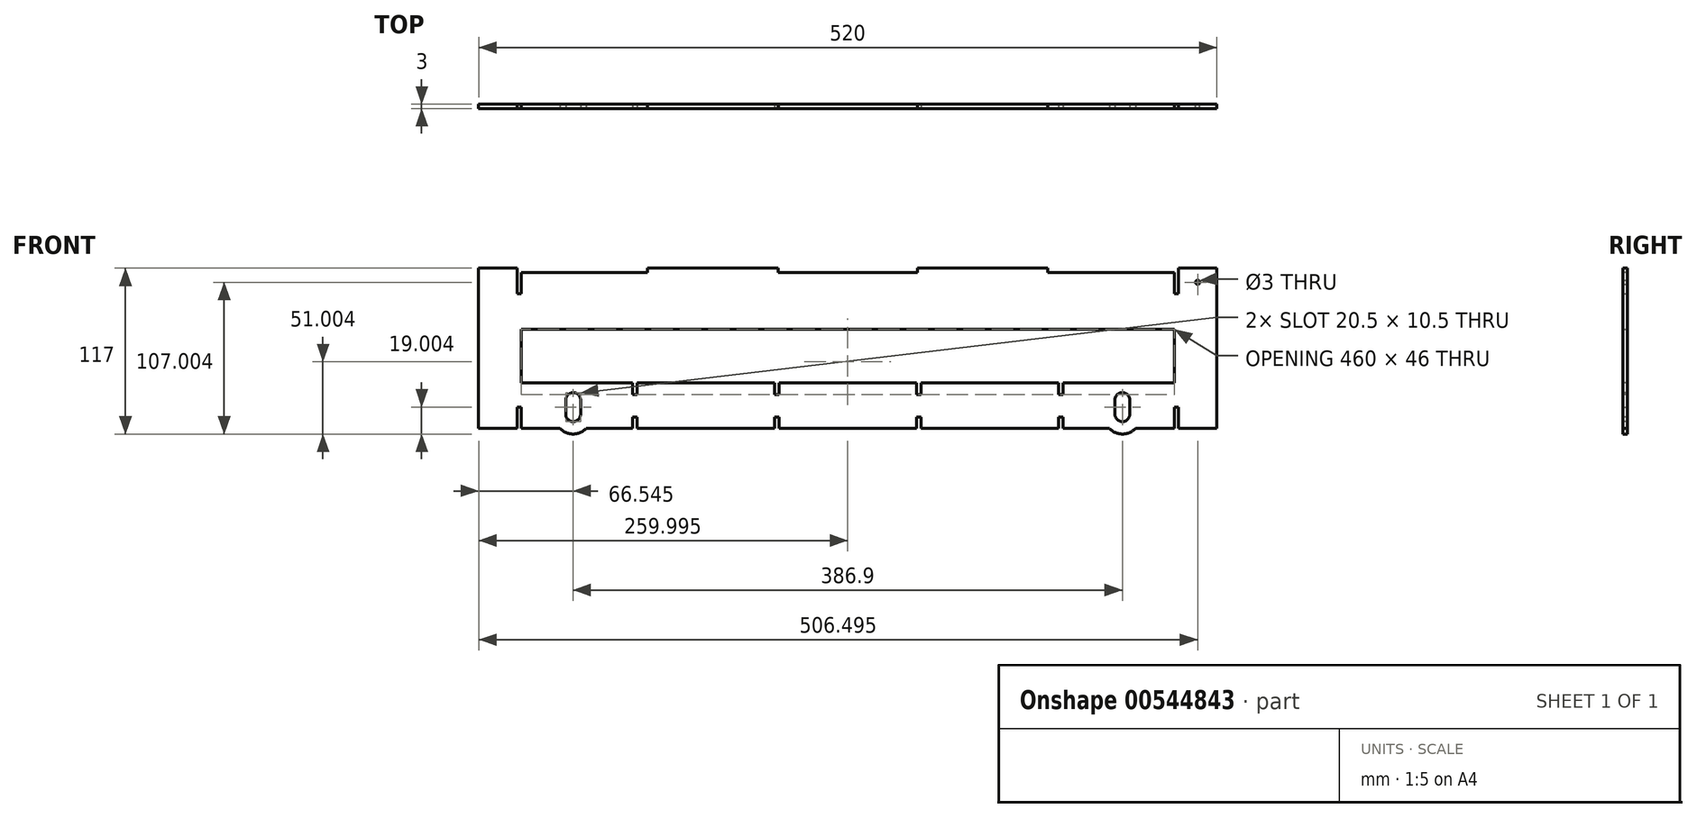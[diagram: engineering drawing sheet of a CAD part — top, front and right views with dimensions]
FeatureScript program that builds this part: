
annotation { "Feature Type Name" : "Feature", "Feature Type Description" : "" }
export const myFeature = defineFeature(function(context is Context, id is Id, definition is map)
    precondition{}
    {
        {
            var Q0;
            Q0=qCreatedBy(makeId("Front.planeOp"),FACE);
            var sketch = newSketch(context, id + "F0", { "sketchPlane" : qUnion([Q0])});
            skLineSegment(sketch, "E0", {"start": v(-316.48, -216.1) * mm, "end": v(-316.48, -106.1) * mm});
            skLineSegment(sketch, "E1", {"start": v(-346.48, -146.1) * mm, "end": v(-346.48, -184.1) * mm});
            skLineSegment(sketch, "E2", {"start": v(-576.48, -216.1) * mm, "end": v(-576.48, -184.1) * mm, "construction": true});
            skPoint(sketch, "E2.endSnap0", {"position": v(-560.36, -184.1) * mm});
            skPoint(sketch, "E3.orphan", {"position": v(-576.48, -200.1) * mm});
            skLineSegment(sketch, "E4.MirrorCS", {"start": v(-806.48, -146.1) * mm, "end": v(-806.48, -184.1) * mm});
            skLineSegment(sketch, "E5.MirrorCS", {"start": v(-836.48, -216.1) * mm, "end": v(-836.48, -106.1) * mm});
            skLineSegment(sketch, "E6", {"start": v(-316.48, -106.1) * mm, "end": v(-343.48, -106.1) * mm});
            skLineSegment(sketch, "E7", {"start": v(-806.48, -146.1) * mm, "end": v(-346.48, -146.1) * mm});
            skLineSegment(sketch, "E8.top", {"start": v(-809.48, -121.1) * mm, "end": v(-806.48, -121.1) * mm});
            skLineSegment(sketch, "E8.left", {"start": v(-809.48, -106.1) * mm, "end": v(-809.48, -121.1) * mm});
            skLineSegment(sketch, "E8.right", {"start": v(-806.48, -106.1) * mm, "end": v(-806.48, -121.1) * mm});
            skLineSegment(sketch, "E9.trimOffspring", {"start": v(-809.48, -106.1) * mm, "end": v(-836.48, -106.1) * mm});
            skLineSegment(sketch, "E10.top", {"start": v(-346.48, -121.1) * mm, "end": v(-343.48, -121.1) * mm});
            skLineSegment(sketch, "E10.left", {"start": v(-346.48, -106.1) * mm, "end": v(-346.48, -121.1) * mm});
            skLineSegment(sketch, "E10.right", {"start": v(-343.48, -106.1) * mm, "end": v(-343.48, -121.1) * mm});
            skLineSegment(sketch, "E11.trimOffspring", {"start": v(-346.48, -106.1) * mm, "end": v(-806.48, -106.1) * mm});
            skLineSegment(sketch, "E12.bottom", {"start": v(-809.48, -201.1) * mm, "end": v(-806.48, -201.1) * mm});
            skLineSegment(sketch, "E12.left", {"start": v(-809.48, -201.1) * mm, "end": v(-809.48, -216.1) * mm});
            skLineSegment(sketch, "E12.right", {"start": v(-806.48, -201.1) * mm, "end": v(-806.48, -216.1) * mm});
            skLineSegment(sketch, "E13.trimOffspring", {"start": v(-809.48, -216.1) * mm, "end": v(-836.48, -216.1) * mm});
            skLineSegment(sketch, "E14.bottom", {"start": v(-343.48, -201.1) * mm, "end": v(-346.48, -201.1) * mm});
            skLineSegment(sketch, "E14.left", {"start": v(-343.48, -201.1) * mm, "end": v(-343.48, -216.1) * mm});
            skLineSegment(sketch, "E14.right", {"start": v(-346.48, -201.1) * mm, "end": v(-346.48, -216.1) * mm});
            skLineSegment(sketch, "E15.trimOffspring", {"start": v(-343.48, -216.1) * mm, "end": v(-316.48, -216.1) * mm});
            skLineSegment(sketch, "E16.trimOffspring", {"start": v(-346.48, -184.1) * mm, "end": v(-806.48, -184.1) * mm});
            skLineSegment(sketch, "E17.trimOffspring", {"start": v(-346.48, -216.1) * mm, "end": v(-806.48, -216.1) * mm});
            skSolve(sketch);
        }
        {
            var Q0;
            Q0 = qSketchRegion(id + "F0", true);
            extrude(context, id + "F1", {"entities" : qUnion([Q0]), "depth" : 3 * mm, "offsetDistance" : 25 * mm});
        }
        {
            var Q0;
            Q0=makeQuery(id+"F1.opExtrude","CAP_FACE",FACE,{"disambiguationData":[OSD([sQuery(id+"F0.wireOp",EDGE,"E0"),sQuery(id+"F0.wireOp",EDGE,"E1"),sQuery(id+"F0.wireOp",EDGE,"E4.MirrorCS"),sQuery(id+"F0.wireOp",EDGE,"E5.MirrorCS"),sQuery(id+"F0.wireOp",EDGE,"E6"),sQuery(id+"F0.wireOp",EDGE,"E7"),sQuery(id+"F0.wireOp",EDGE,"E8.top"),sQuery(id+"F0.wireOp",EDGE,"E8.left"),sQuery(id+"F0.wireOp",EDGE,"E8.right"),sQuery(id+"F0.wireOp",EDGE,"E9.trimOffspring"),sQuery(id+"F0.wireOp",EDGE,"E10.top"),sQuery(id+"F0.wireOp",EDGE,"E10.left"),sQuery(id+"F0.wireOp",EDGE,"E10.right"),sQuery(id+"F0.wireOp",EDGE,"E11.trimOffspring"),sQuery(id+"F0.wireOp",EDGE,"E12.bottom"),sQuery(id+"F0.wireOp",EDGE,"E12.left"),sQuery(id+"F0.wireOp",EDGE,"E12.right"),sQuery(id+"F0.wireOp",EDGE,"E13.trimOffspring"),sQuery(id+"F0.wireOp",EDGE,"E14.bottom"),sQuery(id+"F0.wireOp",EDGE,"E14.left"),sQuery(id+"F0.wireOp",EDGE,"E14.right"),sQuery(id+"F0.wireOp",EDGE,"E15.trimOffspring"),sQuery(id+"F0.wireOp",EDGE,"E16.trimOffspring"),sQuery(id+"F0.wireOp",EDGE,"E17.trimOffspring")])],"isStart":false});
            var sketch = newSketch(context, id + "F2", { "sketchPlane" : qUnion([Q0])});
            skLineSegment(sketch, "E18.bottom", {"start": v(-836.48, -106.1) * mm, "end": v(-836.48, -103.1) * mm});
            skLineSegment(sketch, "E18.top", {"start": v(-809.48, -106.1) * mm, "end": v(-809.48, -103.1) * mm});
            skLineSegment(sketch, "E18.left", {"start": v(-836.48, -106.1) * mm, "end": v(-809.48, -106.1) * mm});
            skLineSegment(sketch, "E18.right", {"start": v(-836.48, -103.1) * mm, "end": v(-809.48, -103.1) * mm});
            skLineSegment(sketch, "E19.bottom", {"start": v(-316.48, -106.1) * mm, "end": v(-316.48, -103.1) * mm});
            skLineSegment(sketch, "E19.top", {"start": v(-343.48, -106.1) * mm, "end": v(-343.48, -103.1) * mm});
            skLineSegment(sketch, "E19.left", {"start": v(-316.48, -106.1) * mm, "end": v(-343.48, -106.1) * mm});
            skLineSegment(sketch, "E19.right", {"start": v(-316.48, -103.1) * mm, "end": v(-343.48, -103.1) * mm});
            skLineSegment(sketch, "E20.bottom", {"start": v(-717.48, -106.1) * mm, "end": v(-717.48, -103.1) * mm});
            skLineSegment(sketch, "E20.top", {"start": v(-625.48, -106.1) * mm, "end": v(-625.48, -103.1) * mm});
            skLineSegment(sketch, "E20.left", {"start": v(-717.48, -106.1) * mm, "end": v(-625.48, -106.1) * mm});
            skLineSegment(sketch, "E20.right", {"start": v(-717.48, -103.1) * mm, "end": v(-625.48, -103.1) * mm});
            skLineSegment(sketch, "E21.bottom", {"start": v(-527.48, -103.1) * mm, "end": v(-527.48, -106.1) * mm});
            skLineSegment(sketch, "E21.top", {"start": v(-435.48, -103.1) * mm, "end": v(-435.48, -106.1) * mm});
            skLineSegment(sketch, "E21.left", {"start": v(-527.48, -103.1) * mm, "end": v(-435.48, -103.1) * mm});
            skLineSegment(sketch, "E21.right", {"start": v(-527.48, -106.1) * mm, "end": v(-435.48, -106.1) * mm});
            skSolve(sketch);
        }
        {
            var Q0;
            Q0 = qSketchRegion(id + "F2", true);
            extrude(context, id + "F3", {"entities" : qUnion([Q0]), "operationType" : NewBodyOperationType.ADD, "oppositeDirection" : true, "depth" : 3 * mm, "offsetDistance" : 25 * mm});
        }
        {
            var Q0;
            Q0=makeQuery(id+"F3.boolean.opBoolean","MERGE",FACE,{"derivedFrom":[makeQuery(id+"F1.opExtrude","CAP_FACE",FACE,{"disambiguationData":[OSD([sQuery(id+"F0.wireOp",EDGE,"E0"),sQuery(id+"F0.wireOp",EDGE,"E1"),sQuery(id+"F0.wireOp",EDGE,"E4.MirrorCS"),sQuery(id+"F0.wireOp",EDGE,"E5.MirrorCS"),sQuery(id+"F0.wireOp",EDGE,"E6"),sQuery(id+"F0.wireOp",EDGE,"E7"),sQuery(id+"F0.wireOp",EDGE,"E8.top"),sQuery(id+"F0.wireOp",EDGE,"E8.left"),sQuery(id+"F0.wireOp",EDGE,"E8.right"),sQuery(id+"F0.wireOp",EDGE,"E9.trimOffspring"),sQuery(id+"F0.wireOp",EDGE,"E10.top"),sQuery(id+"F0.wireOp",EDGE,"E10.left"),sQuery(id+"F0.wireOp",EDGE,"E10.right"),sQuery(id+"F0.wireOp",EDGE,"E11.trimOffspring"),sQuery(id+"F0.wireOp",EDGE,"E12.bottom"),sQuery(id+"F0.wireOp",EDGE,"E12.left"),sQuery(id+"F0.wireOp",EDGE,"E12.right"),sQuery(id+"F0.wireOp",EDGE,"E13.trimOffspring"),sQuery(id+"F0.wireOp",EDGE,"E14.bottom"),sQuery(id+"F0.wireOp",EDGE,"E14.left"),sQuery(id+"F0.wireOp",EDGE,"E14.right"),sQuery(id+"F0.wireOp",EDGE,"E15.trimOffspring"),sQuery(id+"F0.wireOp",EDGE,"E16.trimOffspring"),sQuery(id+"F0.wireOp",EDGE,"E17.trimOffspring")])],"isStart":false}),makeQuery(id+"F3.opExtrude","CAP_FACE",FACE,{"disambiguationData":[OSD([sQuery(id+"F2.wireOp",EDGE,"E18.bottom"),sQuery(id+"F2.wireOp",EDGE,"E18.top"),sQuery(id+"F2.wireOp",EDGE,"E18.left"),sQuery(id+"F2.wireOp",EDGE,"E18.right")])],"isStart":true}),makeQuery(id+"F3.opExtrude","CAP_FACE",FACE,{"disambiguationData":[OSD([sQuery(id+"F2.wireOp",EDGE,"E19.bottom"),sQuery(id+"F2.wireOp",EDGE,"E19.top"),sQuery(id+"F2.wireOp",EDGE,"E19.left"),sQuery(id+"F2.wireOp",EDGE,"E19.right")])],"isStart":true}),makeQuery(id+"F3.opExtrude","CAP_FACE",FACE,{"disambiguationData":[OSD([sQuery(id+"F2.wireOp",EDGE,"E20.bottom"),sQuery(id+"F2.wireOp",EDGE,"E20.top"),sQuery(id+"F2.wireOp",EDGE,"E20.left"),sQuery(id+"F2.wireOp",EDGE,"E20.right")])],"isStart":true}),makeQuery(id+"F3.opExtrude","CAP_FACE",FACE,{"disambiguationData":[OSD([sQuery(id+"F2.wireOp",EDGE,"E21.bottom"),sQuery(id+"F2.wireOp",EDGE,"E21.top"),sQuery(id+"F2.wireOp",EDGE,"E21.left"),sQuery(id+"F2.wireOp",EDGE,"E21.right")])],"isStart":true})]});
            var sketch = newSketch(context, id + "F4", { "sketchPlane" : qUnion([Q0])});
            skLineSegment(sketch, "E22", {"start": v(-383.03, -196.1) * mm, "end": v(-383.03, -206.1) * mm, "construction": true});
            skArc(sketch, "E23", {"start": v(-377.78, -196.1) * mm, "mid": v(-383.03, -190.86) * mm, "end": v(-388.28, -196.1) * mm});
            skArc(sketch, "E24", {"start": v(-388.28, -206.1) * mm, "mid": v(-383.03, -211.36) * mm, "end": v(-377.78, -206.1) * mm});
            skLineSegment(sketch, "E25", {"start": v(-383.03, -201.1) * mm, "end": v(-378.15, -201.1) * mm, "construction": true});
            skLineSegment(sketch, "E26", {"start": v(-377.78, -196.1) * mm, "end": v(-377.78, -206.1) * mm});
            skLineSegment(sketch, "E27", {"start": v(-388.28, -196.1) * mm, "end": v(-388.28, -206.1) * mm});
            skLineSegment(sketch, "E28", {"start": v(-769.93, -196.1) * mm, "end": v(-769.93, -206.1) * mm, "construction": true});
            skArc(sketch, "E29", {"start": v(-764.68, -196.1) * mm, "mid": v(-769.93, -190.86) * mm, "end": v(-775.18, -196.1) * mm});
            skArc(sketch, "E30", {"start": v(-775.18, -206.1) * mm, "mid": v(-769.93, -211.36) * mm, "end": v(-764.68, -206.1) * mm});
            skLineSegment(sketch, "E31", {"start": v(-769.93, -201.1) * mm, "end": v(-765.05, -201.1) * mm, "construction": true});
            skLineSegment(sketch, "E32", {"start": v(-764.68, -196.1) * mm, "end": v(-764.68, -206.1) * mm});
            skLineSegment(sketch, "E33", {"start": v(-775.18, -196.1) * mm, "end": v(-775.18, -206.1) * mm});
            skSolve(sketch);
        }
        {
            var Q0;
            Q0 = qSketchRegion(id + "F4", true);
            extrude(context, id + "F5", {"entities" : qUnion([Q0]), "operationType" : NewBodyOperationType.REMOVE, "endBound" : BoundingType.UP_TO_NEXT, "oppositeDirection" : true, "depth" : 25 * mm, "offsetDistance" : 25 * mm});
        }
        {
            var Q0;
            Q0=makeQuery(id+"F3.boolean.opBoolean","MERGE",FACE,{"derivedFrom":[makeQuery(id+"F1.opExtrude","CAP_FACE",FACE,{"disambiguationData":[OSD([sQuery(id+"F0.wireOp",EDGE,"E0"),sQuery(id+"F0.wireOp",EDGE,"E1"),sQuery(id+"F0.wireOp",EDGE,"E4.MirrorCS"),sQuery(id+"F0.wireOp",EDGE,"E5.MirrorCS"),sQuery(id+"F0.wireOp",EDGE,"E6"),sQuery(id+"F0.wireOp",EDGE,"E7"),sQuery(id+"F0.wireOp",EDGE,"E8.top"),sQuery(id+"F0.wireOp",EDGE,"E8.left"),sQuery(id+"F0.wireOp",EDGE,"E8.right"),sQuery(id+"F0.wireOp",EDGE,"E9.trimOffspring"),sQuery(id+"F0.wireOp",EDGE,"E10.top"),sQuery(id+"F0.wireOp",EDGE,"E10.left"),sQuery(id+"F0.wireOp",EDGE,"E10.right"),sQuery(id+"F0.wireOp",EDGE,"E11.trimOffspring"),sQuery(id+"F0.wireOp",EDGE,"E12.bottom"),sQuery(id+"F0.wireOp",EDGE,"E12.left"),sQuery(id+"F0.wireOp",EDGE,"E12.right"),sQuery(id+"F0.wireOp",EDGE,"E13.trimOffspring"),sQuery(id+"F0.wireOp",EDGE,"E14.bottom"),sQuery(id+"F0.wireOp",EDGE,"E14.left"),sQuery(id+"F0.wireOp",EDGE,"E14.right"),sQuery(id+"F0.wireOp",EDGE,"E15.trimOffspring"),sQuery(id+"F0.wireOp",EDGE,"E16.trimOffspring"),sQuery(id+"F0.wireOp",EDGE,"E17.trimOffspring")])],"isStart":false}),makeQuery(id+"F3.opExtrude","CAP_FACE",FACE,{"disambiguationData":[OSD([sQuery(id+"F2.wireOp",EDGE,"E18.bottom"),sQuery(id+"F2.wireOp",EDGE,"E18.top"),sQuery(id+"F2.wireOp",EDGE,"E18.left"),sQuery(id+"F2.wireOp",EDGE,"E18.right")])],"isStart":true}),makeQuery(id+"F3.opExtrude","CAP_FACE",FACE,{"disambiguationData":[OSD([sQuery(id+"F2.wireOp",EDGE,"E19.bottom"),sQuery(id+"F2.wireOp",EDGE,"E19.top"),sQuery(id+"F2.wireOp",EDGE,"E19.left"),sQuery(id+"F2.wireOp",EDGE,"E19.right")])],"isStart":true}),makeQuery(id+"F3.opExtrude","CAP_FACE",FACE,{"disambiguationData":[OSD([sQuery(id+"F2.wireOp",EDGE,"E20.bottom"),sQuery(id+"F2.wireOp",EDGE,"E20.top"),sQuery(id+"F2.wireOp",EDGE,"E20.left"),sQuery(id+"F2.wireOp",EDGE,"E20.right")])],"isStart":true}),makeQuery(id+"F3.opExtrude","CAP_FACE",FACE,{"disambiguationData":[OSD([sQuery(id+"F2.wireOp",EDGE,"E21.bottom"),sQuery(id+"F2.wireOp",EDGE,"E21.top"),sQuery(id+"F2.wireOp",EDGE,"E21.left"),sQuery(id+"F2.wireOp",EDGE,"E21.right")])],"isStart":true})]});
            var sketch = newSketch(context, id + "F6", { "sketchPlane" : qUnion([Q0])});
            skLineSegment(sketch, "E34.bottom", {"start": v(-727.98, -216.1) * mm, "end": v(-727.98, -208.1) * mm});
            skLineSegment(sketch, "E34.top", {"start": v(-724.98, -216.1) * mm, "end": v(-724.98, -208.1) * mm});
            skLineSegment(sketch, "E34.left", {"start": v(-727.98, -216.1) * mm, "end": v(-724.98, -216.1) * mm});
            skLineSegment(sketch, "E34.right", {"start": v(-727.98, -208.1) * mm, "end": v(-724.98, -208.1) * mm});
            skLineSegment(sketch, "E35.bottom", {"start": v(-727.98, -184.1) * mm, "end": v(-727.98, -192.1) * mm});
            skLineSegment(sketch, "E35.top", {"start": v(-724.98, -184.1) * mm, "end": v(-724.98, -192.1) * mm});
            skLineSegment(sketch, "E35.left", {"start": v(-727.98, -184.1) * mm, "end": v(-724.98, -184.1) * mm});
            skLineSegment(sketch, "E35.right", {"start": v(-727.98, -192.1) * mm, "end": v(-724.98, -192.1) * mm});
            skLineSegment(sketch, "E36.0.1.0", {"start": v(-624.98, -184.1) * mm, "end": v(-624.98, -192.1) * mm});
            skLineSegment(sketch, "E36.0.1.1", {"start": v(-627.98, -184.1) * mm, "end": v(-627.98, -192.1) * mm});
            skLineSegment(sketch, "E36.0.1.2", {"start": v(-627.98, -216.1) * mm, "end": v(-627.98, -208.1) * mm});
            skLineSegment(sketch, "E36.0.1.3", {"start": v(-624.98, -216.1) * mm, "end": v(-624.98, -208.1) * mm});
            skLineSegment(sketch, "E36.0.1.4", {"start": v(-627.98, -184.1) * mm, "end": v(-624.98, -184.1) * mm});
            skLineSegment(sketch, "E36.0.1.5", {"start": v(-627.98, -192.1) * mm, "end": v(-624.98, -192.1) * mm});
            skLineSegment(sketch, "E36.0.1.6", {"start": v(-627.98, -216.1) * mm, "end": v(-624.98, -216.1) * mm});
            skLineSegment(sketch, "E36.0.1.7", {"start": v(-627.98, -208.1) * mm, "end": v(-624.98, -208.1) * mm});
            skLineSegment(sketch, "E36.0.2.0", {"start": v(-524.98, -184.1) * mm, "end": v(-524.98, -192.1) * mm});
            skLineSegment(sketch, "E36.0.2.1", {"start": v(-527.98, -184.1) * mm, "end": v(-527.98, -192.1) * mm});
            skLineSegment(sketch, "E36.0.2.2", {"start": v(-527.98, -216.1) * mm, "end": v(-527.98, -208.1) * mm});
            skLineSegment(sketch, "E36.0.2.3", {"start": v(-524.98, -216.1) * mm, "end": v(-524.98, -208.1) * mm});
            skLineSegment(sketch, "E36.0.2.4", {"start": v(-527.98, -184.1) * mm, "end": v(-524.98, -184.1) * mm});
            skLineSegment(sketch, "E36.0.2.5", {"start": v(-527.98, -192.1) * mm, "end": v(-524.98, -192.1) * mm});
            skLineSegment(sketch, "E36.0.2.6", {"start": v(-527.98, -216.1) * mm, "end": v(-524.98, -216.1) * mm});
            skLineSegment(sketch, "E36.0.2.7", {"start": v(-527.98, -208.1) * mm, "end": v(-524.98, -208.1) * mm});
            skLineSegment(sketch, "E36.0.3.0", {"start": v(-424.98, -184.1) * mm, "end": v(-424.98, -192.1) * mm});
            skLineSegment(sketch, "E36.0.3.1", {"start": v(-427.98, -184.1) * mm, "end": v(-427.98, -192.1) * mm});
            skLineSegment(sketch, "E36.0.3.2", {"start": v(-427.98, -216.1) * mm, "end": v(-427.98, -208.1) * mm});
            skLineSegment(sketch, "E36.0.3.3", {"start": v(-424.98, -216.1) * mm, "end": v(-424.98, -208.1) * mm});
            skLineSegment(sketch, "E36.0.3.4", {"start": v(-427.98, -184.1) * mm, "end": v(-424.98, -184.1) * mm});
            skLineSegment(sketch, "E36.0.3.5", {"start": v(-427.98, -192.1) * mm, "end": v(-424.98, -192.1) * mm});
            skLineSegment(sketch, "E36.0.3.6", {"start": v(-427.98, -216.1) * mm, "end": v(-424.98, -216.1) * mm});
            skLineSegment(sketch, "E36.0.3.7", {"start": v(-427.98, -208.1) * mm, "end": v(-424.98, -208.1) * mm});
            skLineSegment(sketch, "E36.direction1", {"start": v(-724.98, -216.1) * mm, "end": v(-724.98, -191.1) * mm, "construction": true});
            skLineSegment(sketch, "E36.direction2", {"start": v(-724.98, -216.1) * mm, "end": v(-624.98, -216.1) * mm, "construction": true});
            skLineSegment(sketch, "E37", {"start": v(-836.48, -196.82) * mm, "end": v(-836.48, -216.1) * mm, "construction": true});
            skLineSegment(sketch, "E38", {"start": v(-836.48, -216.1) * mm, "end": v(-822.98, -216.1) * mm, "construction": true});
            skSolve(sketch);
        }
        {
            var Q0;
            Q0 = qSketchRegion(id + "F6", true);
            extrude(context, id + "F7", {"entities" : qUnion([Q0]), "operationType" : NewBodyOperationType.REMOVE, "oppositeDirection" : true, "depth" : 3 * mm, "offsetDistance" : 25 * mm});
        }
        {
            var Q0;
            Q0=makeQuery(id+"F3.boolean.opBoolean","MERGE",FACE,{"derivedFrom":[makeQuery(id+"F1.opExtrude","CAP_FACE",FACE,{"disambiguationData":[OSD([sQuery(id+"F0.wireOp",EDGE,"E0"),sQuery(id+"F0.wireOp",EDGE,"E1"),sQuery(id+"F0.wireOp",EDGE,"E4.MirrorCS"),sQuery(id+"F0.wireOp",EDGE,"E5.MirrorCS"),sQuery(id+"F0.wireOp",EDGE,"E6"),sQuery(id+"F0.wireOp",EDGE,"E7"),sQuery(id+"F0.wireOp",EDGE,"E8.top"),sQuery(id+"F0.wireOp",EDGE,"E8.left"),sQuery(id+"F0.wireOp",EDGE,"E8.right"),sQuery(id+"F0.wireOp",EDGE,"E9.trimOffspring"),sQuery(id+"F0.wireOp",EDGE,"E10.top"),sQuery(id+"F0.wireOp",EDGE,"E10.left"),sQuery(id+"F0.wireOp",EDGE,"E10.right"),sQuery(id+"F0.wireOp",EDGE,"E11.trimOffspring"),sQuery(id+"F0.wireOp",EDGE,"E12.bottom"),sQuery(id+"F0.wireOp",EDGE,"E12.left"),sQuery(id+"F0.wireOp",EDGE,"E12.right"),sQuery(id+"F0.wireOp",EDGE,"E13.trimOffspring"),sQuery(id+"F0.wireOp",EDGE,"E14.bottom"),sQuery(id+"F0.wireOp",EDGE,"E14.left"),sQuery(id+"F0.wireOp",EDGE,"E14.right"),sQuery(id+"F0.wireOp",EDGE,"E15.trimOffspring"),sQuery(id+"F0.wireOp",EDGE,"E16.trimOffspring"),sQuery(id+"F0.wireOp",EDGE,"E17.trimOffspring")])],"isStart":false}),makeQuery(id+"F3.opExtrude","CAP_FACE",FACE,{"disambiguationData":[OSD([sQuery(id+"F2.wireOp",EDGE,"E18.bottom"),sQuery(id+"F2.wireOp",EDGE,"E18.top"),sQuery(id+"F2.wireOp",EDGE,"E18.left"),sQuery(id+"F2.wireOp",EDGE,"E18.right")])],"isStart":true}),makeQuery(id+"F3.opExtrude","CAP_FACE",FACE,{"disambiguationData":[OSD([sQuery(id+"F2.wireOp",EDGE,"E19.bottom"),sQuery(id+"F2.wireOp",EDGE,"E19.top"),sQuery(id+"F2.wireOp",EDGE,"E19.left"),sQuery(id+"F2.wireOp",EDGE,"E19.right")])],"isStart":true}),makeQuery(id+"F3.opExtrude","CAP_FACE",FACE,{"disambiguationData":[OSD([sQuery(id+"F2.wireOp",EDGE,"E20.bottom"),sQuery(id+"F2.wireOp",EDGE,"E20.top"),sQuery(id+"F2.wireOp",EDGE,"E20.left"),sQuery(id+"F2.wireOp",EDGE,"E20.right")])],"isStart":true}),makeQuery(id+"F3.opExtrude","CAP_FACE",FACE,{"disambiguationData":[OSD([sQuery(id+"F2.wireOp",EDGE,"E21.bottom"),sQuery(id+"F2.wireOp",EDGE,"E21.top"),sQuery(id+"F2.wireOp",EDGE,"E21.left"),sQuery(id+"F2.wireOp",EDGE,"E21.right")])],"isStart":true})]});
            var sketch = newSketch(context, id + "F8", { "sketchPlane" : qUnion([Q0])});
            skLineSegment(sketch, "E39", {"start": v(-779.1, -216.1) * mm, "end": v(-760.77, -216.1) * mm});
            skArc(sketch, "E40.trimOffspring", {"start": v(-779.1, -216.1) * mm, "mid": v(-769.93, -220.1) * mm, "end": v(-760.77, -216.1) * mm});
            skLineSegment(sketch, "E41", {"start": v(-392.2, -216.1) * mm, "end": v(-373.87, -216.1) * mm});
            skArc(sketch, "E42.trimOffspring", {"start": v(-392.2, -216.1) * mm, "mid": v(-383.03, -220.1) * mm, "end": v(-373.87, -216.1) * mm});
            skSolve(sketch);
        }
        {
            var Q0;
            Q0 = qSketchRegion(id + "F8", true);
            extrude(context, id + "F9", {"entities" : qUnion([Q0]), "operationType" : NewBodyOperationType.ADD, "oppositeDirection" : true, "depth" : 3 * mm, "offsetDistance" : 25 * mm});
        }
        {
            var Q0;
            Q0=makeQuery(id+"F9.boolean.opBoolean","MERGE",FACE,{"derivedFrom":[makeQuery(id+"F3.boolean.opBoolean","MERGE",FACE,{"derivedFrom":[makeQuery(id+"F1.opExtrude","CAP_FACE",FACE,{"disambiguationData":[OSD([sQuery(id+"F0.wireOp",EDGE,"E0"),sQuery(id+"F0.wireOp",EDGE,"E1"),sQuery(id+"F0.wireOp",EDGE,"E4.MirrorCS"),sQuery(id+"F0.wireOp",EDGE,"E5.MirrorCS"),sQuery(id+"F0.wireOp",EDGE,"E6"),sQuery(id+"F0.wireOp",EDGE,"E7"),sQuery(id+"F0.wireOp",EDGE,"E8.top"),sQuery(id+"F0.wireOp",EDGE,"E8.left"),sQuery(id+"F0.wireOp",EDGE,"E8.right"),sQuery(id+"F0.wireOp",EDGE,"E9.trimOffspring"),sQuery(id+"F0.wireOp",EDGE,"E10.top"),sQuery(id+"F0.wireOp",EDGE,"E10.left"),sQuery(id+"F0.wireOp",EDGE,"E10.right"),sQuery(id+"F0.wireOp",EDGE,"E11.trimOffspring"),sQuery(id+"F0.wireOp",EDGE,"E12.bottom"),sQuery(id+"F0.wireOp",EDGE,"E12.left"),sQuery(id+"F0.wireOp",EDGE,"E12.right"),sQuery(id+"F0.wireOp",EDGE,"E13.trimOffspring"),sQuery(id+"F0.wireOp",EDGE,"E14.bottom"),sQuery(id+"F0.wireOp",EDGE,"E14.left"),sQuery(id+"F0.wireOp",EDGE,"E14.right"),sQuery(id+"F0.wireOp",EDGE,"E15.trimOffspring"),sQuery(id+"F0.wireOp",EDGE,"E16.trimOffspring"),sQuery(id+"F0.wireOp",EDGE,"E17.trimOffspring")])],"isStart":true}),makeQuery(id+"F3.opExtrude","CAP_FACE",FACE,{"disambiguationData":[OSD([sQuery(id+"F2.wireOp",EDGE,"E18.bottom"),sQuery(id+"F2.wireOp",EDGE,"E18.top"),sQuery(id+"F2.wireOp",EDGE,"E18.left"),sQuery(id+"F2.wireOp",EDGE,"E18.right")])],"isStart":false}),makeQuery(id+"F3.opExtrude","CAP_FACE",FACE,{"disambiguationData":[OSD([sQuery(id+"F2.wireOp",EDGE,"E19.bottom"),sQuery(id+"F2.wireOp",EDGE,"E19.top"),sQuery(id+"F2.wireOp",EDGE,"E19.left"),sQuery(id+"F2.wireOp",EDGE,"E19.right")])],"isStart":false}),makeQuery(id+"F3.opExtrude","CAP_FACE",FACE,{"disambiguationData":[OSD([sQuery(id+"F2.wireOp",EDGE,"E20.bottom"),sQuery(id+"F2.wireOp",EDGE,"E20.top"),sQuery(id+"F2.wireOp",EDGE,"E20.left"),sQuery(id+"F2.wireOp",EDGE,"E20.right")])],"isStart":false}),makeQuery(id+"F3.opExtrude","CAP_FACE",FACE,{"disambiguationData":[OSD([sQuery(id+"F2.wireOp",EDGE,"E21.bottom"),sQuery(id+"F2.wireOp",EDGE,"E21.top"),sQuery(id+"F2.wireOp",EDGE,"E21.left"),sQuery(id+"F2.wireOp",EDGE,"E21.right")])],"isStart":false})]}),makeQuery(id+"F9.opExtrude","CAP_FACE",FACE,{"disambiguationData":[OSD([sQuery(id+"F8.wireOp",EDGE,"E39"),sQuery(id+"F8.wireOp",EDGE,"E40.trimOffspring")])],"isStart":false}),makeQuery(id+"F9.opExtrude","CAP_FACE",FACE,{"disambiguationData":[OSD([sQuery(id+"F8.wireOp",EDGE,"E41"),sQuery(id+"F8.wireOp",EDGE,"E42.trimOffspring")])],"isStart":false})]});
            var sketch = newSketch(context, id + "F10", { "sketchPlane" : qUnion([Q0])});
            skCircle(sketch, "E43", {"center": v(329.98, -113.1) * mm, "radius": 2.92 * mm});
            skSolve(sketch);
        }
        {
            var Q0;
            Q0=sQuery(id+"F10.wireOp",VERTEX,"E43.center");
            var Q1;
            Q1=makeQuery(id+"F1.opExtrude","SWEPT_BODY",BODY,{"disambiguationData":[OSD([sQuery(id+"F0.wireOp",EDGE,"E0"),sQuery(id+"F0.wireOp",EDGE,"E1"),sQuery(id+"F0.wireOp",EDGE,"E4.MirrorCS"),sQuery(id+"F0.wireOp",EDGE,"E5.MirrorCS"),sQuery(id+"F0.wireOp",EDGE,"E6"),sQuery(id+"F0.wireOp",EDGE,"E7"),sQuery(id+"F0.wireOp",EDGE,"E8.top"),sQuery(id+"F0.wireOp",EDGE,"E8.left"),sQuery(id+"F0.wireOp",EDGE,"E8.right"),sQuery(id+"F0.wireOp",EDGE,"E9.trimOffspring"),sQuery(id+"F0.wireOp",EDGE,"E10.top"),sQuery(id+"F0.wireOp",EDGE,"E10.left"),sQuery(id+"F0.wireOp",EDGE,"E10.right"),sQuery(id+"F0.wireOp",EDGE,"E11.trimOffspring"),sQuery(id+"F0.wireOp",EDGE,"E12.bottom"),sQuery(id+"F0.wireOp",EDGE,"E12.left"),sQuery(id+"F0.wireOp",EDGE,"E12.right"),sQuery(id+"F0.wireOp",EDGE,"E13.trimOffspring"),sQuery(id+"F0.wireOp",EDGE,"E14.bottom"),sQuery(id+"F0.wireOp",EDGE,"E14.left"),sQuery(id+"F0.wireOp",EDGE,"E14.right"),sQuery(id+"F0.wireOp",EDGE,"E15.trimOffspring"),sQuery(id+"F0.wireOp",EDGE,"E16.trimOffspring"),sQuery(id+"F0.wireOp",EDGE,"E17.trimOffspring")])]});
            hole(context, id + "F11", {"style" : HoleStyle.SIMPLE, "endStyle" : HoleEndStyle.THROUGH, "holeDiameter" : 3 * mm, "isTappedThrough" : true, "tappedDepth" : 12 * mm, "tapClearance" : 3, "locations" : qUnion([Q0]), "scope" : qUnion([Q1])});
        }
    });
